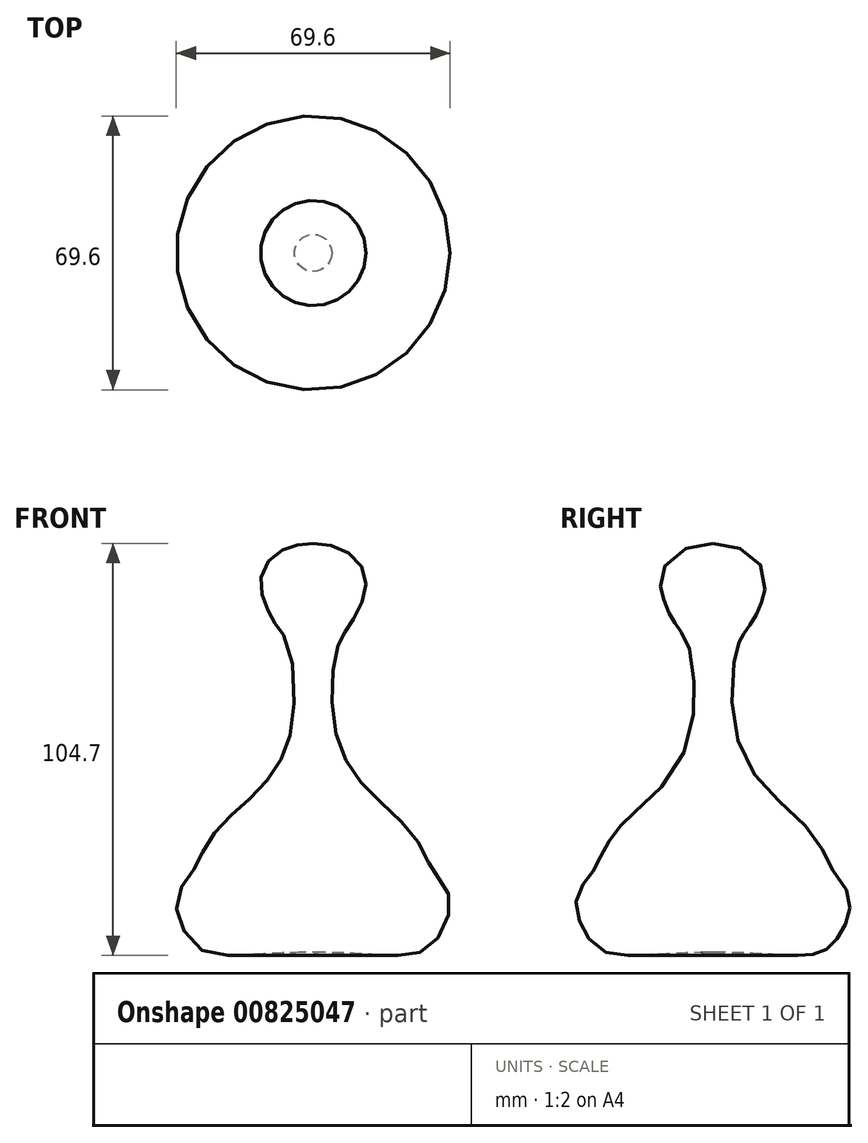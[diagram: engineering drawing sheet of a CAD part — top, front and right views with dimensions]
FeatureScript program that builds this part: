
annotation { "Feature Type Name" : "Feature", "Feature Type Description" : "" }
export const myFeature = defineFeature(function(context is Context, id is Id, definition is map)
    precondition{}
    {
        {
            var Q0;
            Q0=qCreatedBy(makeId("Front.planeOp"),FACE);
            var sketch = newSketch(context, id + "F0", { "sketchPlane" : qUnion([Q0])});
            skLineSegment(sketch, "E0", {"start": v(0, 76.35) * mm, "end": v(0, -77.07) * mm});
            skFitSpline(sketch, "E1", {"points": [v(0, 45.59) * mm, v(7.48, 44.04) * mm, v(12.96, 38.28) * mm, v(12.38, 30.78) * mm, v(8.92, 24.15) * mm, v(6.33, 19.83) * mm, v(5.27, 0) * mm, v(12.82, -15.9) * mm, v(25.4, -28.47) * mm, v(31.05, -38.53) * mm, v(34.74, -44.82) * mm, v(29.8, -56.77) * mm, v(18.54, -59.03) * mm, v(5.34, -58.4) * mm, v(0, -58.4) * mm], "startDerivative": vector(125.45, -9.65) * mm, "endDerivative": vector(-91.73, -1.8) * mm});
            skSolve(sketch);
        }
        {
            var Q0;
            {var subQ0=sQuery(id+"F0.wireOp",EDGE,"E1");Q0=makeQuery(id+"F0.imprint","IMPRINT",FACE,{"disambiguationData":[TD([[makeQuery(id+"F0.imprint","IMPRINT",EDGE,{"derivedFrom":subQ0}),-1.0]])]});}
            var Q1;
            Q1=sQuery(id+"F0.wireOp",EDGE,"E0");
            revolve(context, id + "F1", {"surfaceOperationType" : NewSurfaceOperationType.NEW, "entities" : qUnion([Q0]), "axis" : qUnion([Q1]), "revolveType" : RevolveType.FULL});
        }
    });
